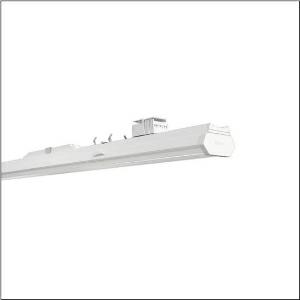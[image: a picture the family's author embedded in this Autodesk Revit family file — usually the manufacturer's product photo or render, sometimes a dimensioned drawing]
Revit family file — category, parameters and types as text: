
# Revit family: licross_r__11_protected_ho_51tp13dn4f5s_0b0f
name_source: partatom
category: Lighting Fixtures
units: mm (PartAtom-declared; Revit-internal decimal feet)

## family parameters
Cut with Voids When Loaded = No
Host = Face
Light Source = No
Part Type = Normal
Room Calculation Point = No
Round Connector Dimension = Use Diameter
Shared = No

## types (1)
- --- (1 x LED, 15550 lm, 87.3 W, 4000K)
    Apparent Load = 87 VA
    CIE Flux Codes = 89 96 99 100 99
    Color Rendering = 80
    Color Temperature = 4000K
    Default Elevation = 1800 mm
    Description = Licross® 11 Protected HO, luminaire insert, of sheet steel, galvanised, coil coated, white, length: 1.500mm, width: 90mm, height: 101mm, LED rated luminous flux: 15.550lm, light colour: 840, control gear: DALI 2, control gear: ECG DALI, with plug, 5-pole, with phase selection, mains connection: 220..240V, AC, 50/60Hz, halogen-free wiring, primary light control with lens, of plastic, primary optical cover: cover, of PMMA, light emission: direct with ceiling illumination distribution, primary light characteristic: symmetric, protection rating (complete): IP64, insulation class (complete): insulation class I (protective earthing), certification: CE, ENEC, VDE, UKCA, protection symbol: D if used in an environment with conductive dust loads with corresponding accessories, impact resistance: IK06, permissible ambient temperature for indoor applications: -25..+30°C, corresponds to IFS (International Featured Standards) requirements for safety and quality in the food industry, reducing of maximum allowable ambient temperature of 5°C with ceiling mounting, LABS conformity tested according to VDMA 24364:2018-05, packaging unit: 1 piece
    Height = 92 mm
    Lamp = 1 x LED
    Lamp Light Flux = 15550 lm
    Lamp Power = 87.3 W
    Lamp count = 1
    Length = 1500 mm
    Luminous efficacy = 178 lm/W
    Manufacturer = Siteco
    ModVariant = No
    Model = 51TP13DN4F5S
    Mounting Place = Ceiling
    Mounting Type = Pendant
    Number of Poles = 1
    OnlyDefault = Yes
    Power Factor = 1
    Product Name = Licross® 11 Protected HO
    Product group = luminaire insert
    ProductGroupID = 902
    Protection Class = Protection class I
    Protection Degree = IP 64
    RLX_Detail_Level = 1
    RlxData = <blob elided: 24317 chars, md5=61670189>
    Socket = socket
    Standby Power = 0 W
    System Light Flux = 15550 lm
    System Power = 87 W
    Type Comments = factory setting: luminous flux: 100 % | dim-lin: 254 | 589 mA
    Type Image = l_1256148.jpg
    URL = http://relux.com
    VarID = @adj_009997
    Voltage = 0 V
    Weight = 0.00 kg
    Width = 88 mm

## geometry (parser evidence)
native form markers: Blend x4, Sweep x12
no freeform markers — native parametric forms only
